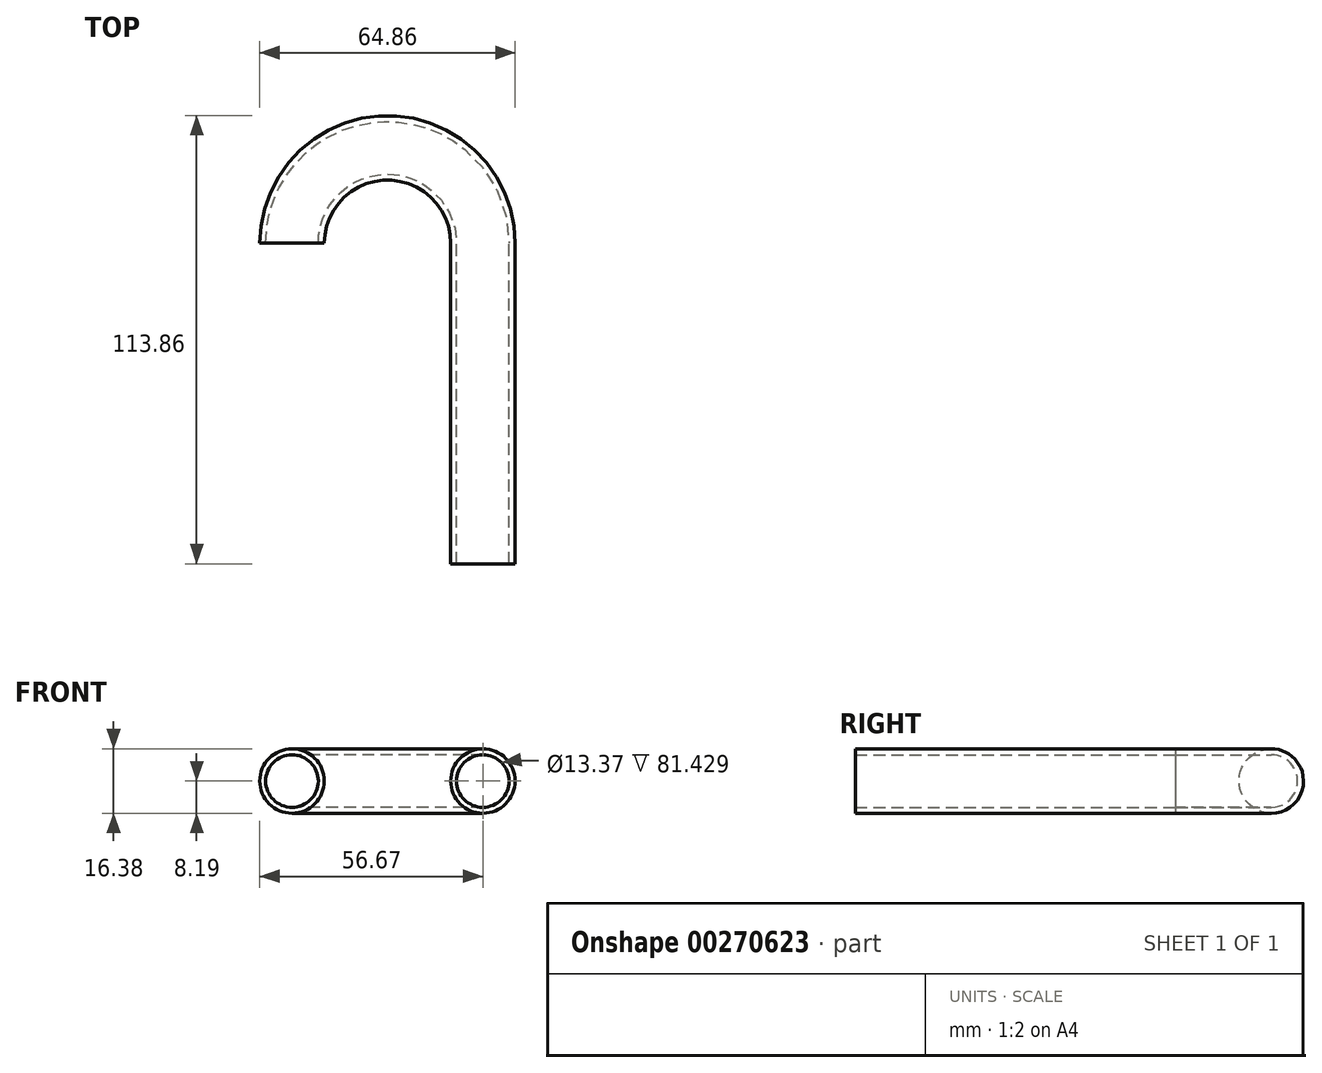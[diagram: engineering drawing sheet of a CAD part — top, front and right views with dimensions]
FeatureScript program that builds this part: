
annotation { "Feature Type Name" : "Feature", "Feature Type Description" : "" }
export const myFeature = defineFeature(function(context is Context, id is Id, definition is map)
    precondition{}
    {
        {
            var Q0;
            Q0=qCreatedBy(makeId("Front.planeOp"),FACE);
            var sketch = newSketch(context, id + "F0", { "sketchPlane" : qUnion([Q0])});
            skCircle(sketch, "E0", {"center": v(0, 0) * mm, "radius": 8.19 * mm});
            skCircle(sketch, "E1", {"center": v(0, 0) * mm, "radius": 6.68 * mm});
            skSolve(sketch);
        }
        {
            var Q0;
            Q0=qCreatedBy(makeId("Top.planeOp"),FACE);
            var sketch = newSketch(context, id + "F1", { "sketchPlane" : qUnion([Q0])});
            skLineSegment(sketch, "E2", {"start": v(0, 0) * mm, "end": v(0, 81.43) * mm});
            skArc(sketch, "E3", {"start": v(0, 81.43) * mm, "mid": v(-24.24, 105.67) * mm, "end": v(-48.49, 81.43) * mm});
            skSolve(sketch);
        }
        {
            var Q0;
            Q0=makeQuery(id+"F0.imprint","IMPRINT",FACE,{"disambiguationData":[TD([[makeQuery(id+"F0.imprint","IMPRINT",EDGE,{"derivedFrom":sQuery(id+"F0.wireOp",EDGE,"E0")}),1.0]])]});
            var Q1;
            Q1=sQuery(id+"F1.wireOp",EDGE,"E2");
            var Q2;
            Q2=sQuery(id+"F1.wireOp",EDGE,"E3");
            sweep(context, id + "F2", {"profiles" : qUnion([Q0]), "path" : qUnion([Q1, Q2])});
        }
    });
